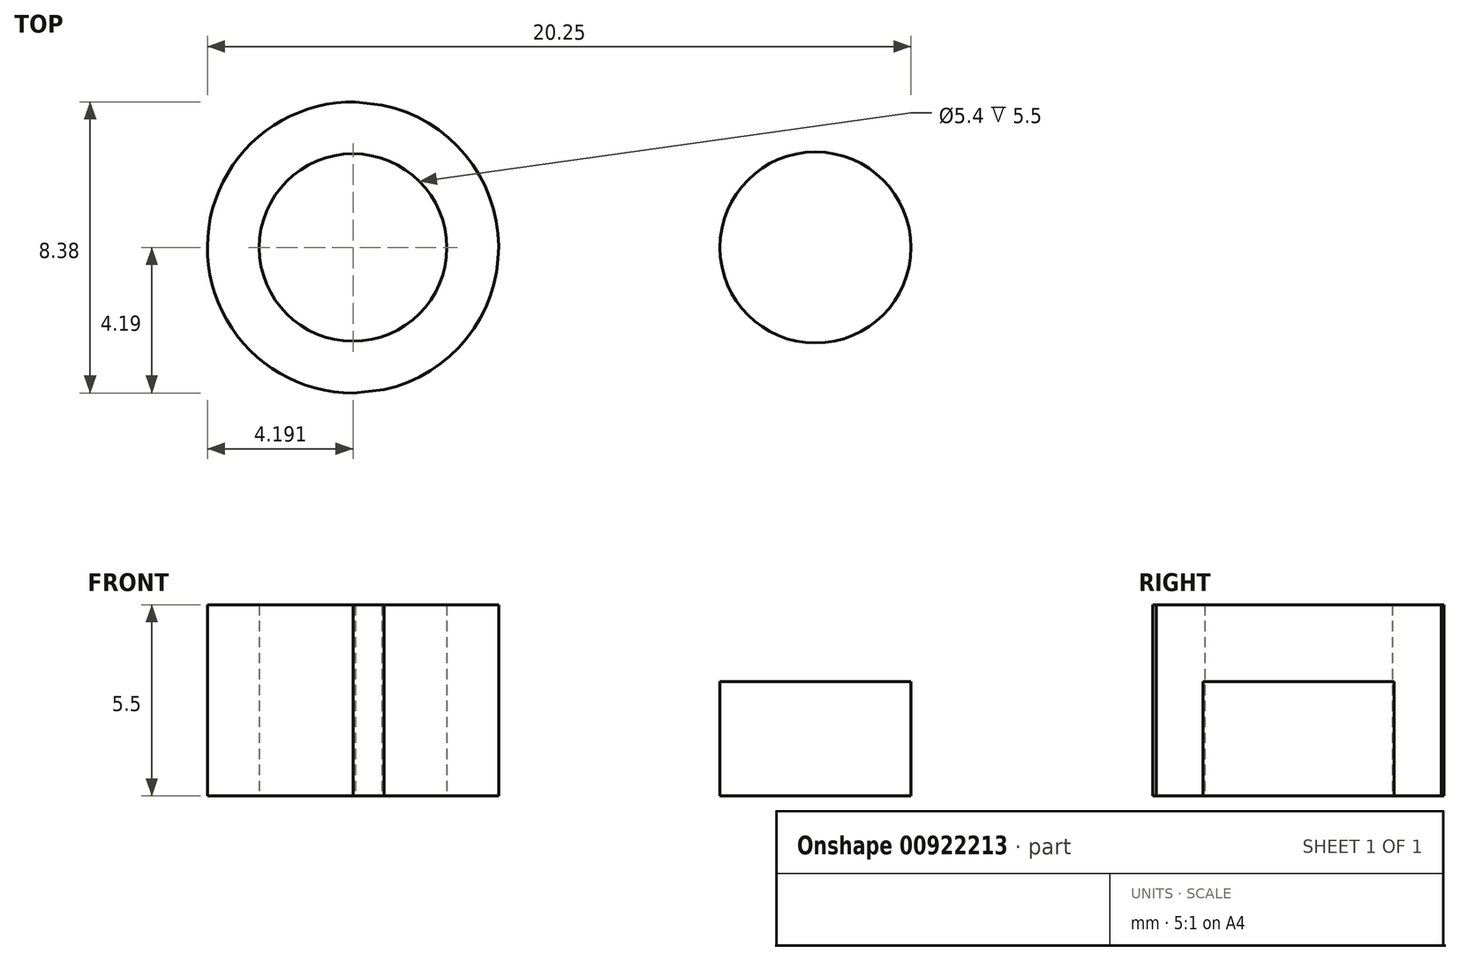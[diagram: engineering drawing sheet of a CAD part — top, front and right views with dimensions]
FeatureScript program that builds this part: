
annotation { "Feature Type Name" : "Feature", "Feature Type Description" : "" }
export const myFeature = defineFeature(function(context is Context, id is Id, definition is map)
    precondition{}
    {
        {
            var Q0;
            Q0=qCreatedBy(makeId("Top.planeOp"),FACE);
            var sketch = newSketch(context, id + "F0", { "sketchPlane" : qUnion([Q0])});
            skCircle(sketch, "E0", {"center": v(5.43, 9.53) * mm, "radius": 4.2 * mm});
            skCircle(sketch, "E1", {"center": v(18.74, 9.53) * mm, "radius": 2.75 * mm});
            skLineSegment(sketch, "E2", {"start": v(1.24, 9.53) * mm, "end": v(21.5, 9.53) * mm, "construction": true});
            skLineSegment(sketch, "E3", {"start": v(5.5, 13.72) * mm, "end": v(18.77, 12.28) * mm});
            skLineSegment(sketch, "E4", {"start": v(5.43, 9.53) * mm, "end": v(5.43, 5.34) * mm, "construction": true});
            skLineSegment(sketch, "E5", {"start": v(5.43, 9.53) * mm, "end": v(5.43, 13.72) * mm, "construction": true});
            skLineSegment(sketch, "E6", {"start": v(18.74, 9.53) * mm, "end": v(18.74, 6.78) * mm, "construction": true});
            skLineSegment(sketch, "E7", {"start": v(18.74, 9.53) * mm, "end": v(18.77, 12.28) * mm, "construction": true});
            skLineSegment(sketch, "E8", {"start": v(5.43, 5.34) * mm, "end": v(18.74, 6.78) * mm});
            skCircle(sketch, "E9.0", {"center": v(5.43, 9.53) * mm, "radius": 2.7 * mm});
            skSolve(sketch);
        }
        {
            var Q0;
            {var subQ0=sQuery(id+"F0.wireOp",EDGE,"E3");var subQ1=sQuery(id+"F0.wireOp",EDGE,"E0");var subQ2=makeQuery(id+"F0.imprint","INTERSECT",VERTEX,{"disambiguationData":[OD(1.0)],"derivedFrom":[subQ1,subQ0]});Q0=makeQuery(id+"F0.imprint","IMPRINT",FACE,{"disambiguationData":[TD([[makeQuery(id+"F0.imprint","IMPRINT",EDGE,{"disambiguationData":[TD([[subQ2,1.0]])],"derivedFrom":subQ1}),-1.0]])]});}
            var Q1;
            {var subQ0=sQuery(id+"F0.wireOp",EDGE,"E1");var subQ1=makeQuery(id+"F0.imprint","INTERSECT",VERTEX,{"derivedFrom":[subQ0,sQuery(id+"F0.wireOp",EDGE,"E3")]});Q1=makeQuery(id+"F0.imprint","IMPRINT",FACE,{"disambiguationData":[TD([[makeQuery(id+"F0.imprint","IMPRINT",EDGE,{"disambiguationData":[TD([[subQ1,-1.0]])],"derivedFrom":subQ0}),1.0]])]});}
            extrude(context, id + "F1", {"entities" : qUnion([Q0, Q1]), "depth" : 3.3 * mm, "offsetDistance" : 25 * mm});
        }
        {
            var Q0;
            Q0=makeQuery(id+"F0.imprint","IMPRINT",FACE,{"disambiguationData":[TD([[makeQuery(id+"F0.imprint","IMPRINT",EDGE,{"derivedFrom":sQuery(id+"F0.wireOp",EDGE,"E9.0")}),-1.0]])]});
            extrude(context, id + "F2", {"entities" : qUnion([Q0]), "operationType" : NewBodyOperationType.ADD, "depth" : 5.5 * mm, "offsetDistance" : 25 * mm});
        }
    });
